# Revit family: KEUCO_14972010100
name_source: partatom
category: Möbel
revit_build: Autodesk Revit 2016 (Build: 20150220_1215(x64)
units: mm (PartAtom-declared; Revit-internal decimal feet)

## family parameters
Arbeitsebenenbasiert = Nein
Beim Laden mit Abzugskörper schneiden = Nein
Gemeinsam genutzt = Nein
Immer vertikal = Ja
Raumberechnungspunkt = Nein

## types (3) — shared parameters
Gewicht = 0.628
Hersteller = KEUCO
Kategorie = ACC
Preisgruppe = 1
Serie = Plan
URL = https://www.keuco.com
Verwendung = GWC / WC

## per-type parameters (varying)
| type | Ausschreibungstext | Beschreibung | Material Abdeckung | Material Bürste |
| 14972070100 | KEUCO PLAN Toilettenbürstengarnitur 14972070100
Toilettenbürstengarnitur aus hochwertigem Edelstahl 
in ästhetischem, funktionalem Design, Wandmodell
komplett mit Kunststoff-Einsatz schwarz,
sowie Bürste mit Griff und Ersatzbürstenkopf schwarz
herausnehmbarer Kunststoff-Einsatz schwarz für leichtes Reinigen
Höhe 135 mm (Höhe inklusive Bürste 399 mm).
Durchmesser 90 mm, Ausladung 95 mm
Die Toilettenbürstengarnitur wird verdeckt angebracht
Lieferung inkl. korrosionsfreiem Befestigungsmaterial | komplett mit Kunststoff-Einsatz schwarz,
Bürste mit Griff und Ersatzbürstenkopf schwarz | Kunstoff-Einsatz weiß | Verchromt |
| 14972010100 | KEUCO PLAN Toilettenbürstengarnitur 14972010100
Hochglanzverchromte Toilettenbürstengarnitur 
in ästhetischem, funktionalem Design, Wandmodell, 
komplett mit Kunststoff-Einsatz weiß 
sowie Bürste mit Griff und Ersatzbürstenkopf weiß
herausnehmbarer Kunststoffeinsatz für leichtes Reinigen
Höhe 135 mm (Höhe inklusive Bürste 399 mm), 
Durchmesser 90 mm, Ausladung 95 mm
Die Toilettenbürstengarnitur wird verdeckt angebracht
Lieferung inkl. korrosionsfreiem Befestigungsmaterial | komplett mit Kunststoff-Einsatz weiß,
Bürste mit Griff und Ersatzbürstenkopf weiß | Kunstoff-Einsatz weiß | Verchromt |
| 14972070200 | KEUCO PLAN Toilettenbürstengarnitur 14972010200
Hochglanzverchromte Toilettenbürstengarnitur 
in ästhetischem, funktionalem Design, Wandmodell
komplett mit Kunststoff-Einsatz schwarz, 
sowie Bürste mit Griff und Ersatzbürstenkopf schwarz
herausnehmbarer Kunststoffeinsatz für leichtes Reinigen
Höhe 135 mm (Höhe inklusive Bürste 399 mm).
Durchmesser 90 mm, Ausladung 95 mm
Die Toilettenbürstengarnitur wird verdeckt angebracht
Lieferung inkl. korrosionsfreiem Befestigungsmaterial | komplett mit Kunststoff-Einsatz schwarz,
Bürste mit Griff und Ersatzbürstenkopf schwarz | Kunstoff-Einsatz Schwarz | Aluminium silber-eloxiert (E6 EV1) |

note: column(s) folded — value = type name in every type: Artikelnummer

## geometry (parser evidence)
native form markers: Blend x2, Sweep x3
no freeform markers — native parametric forms only
